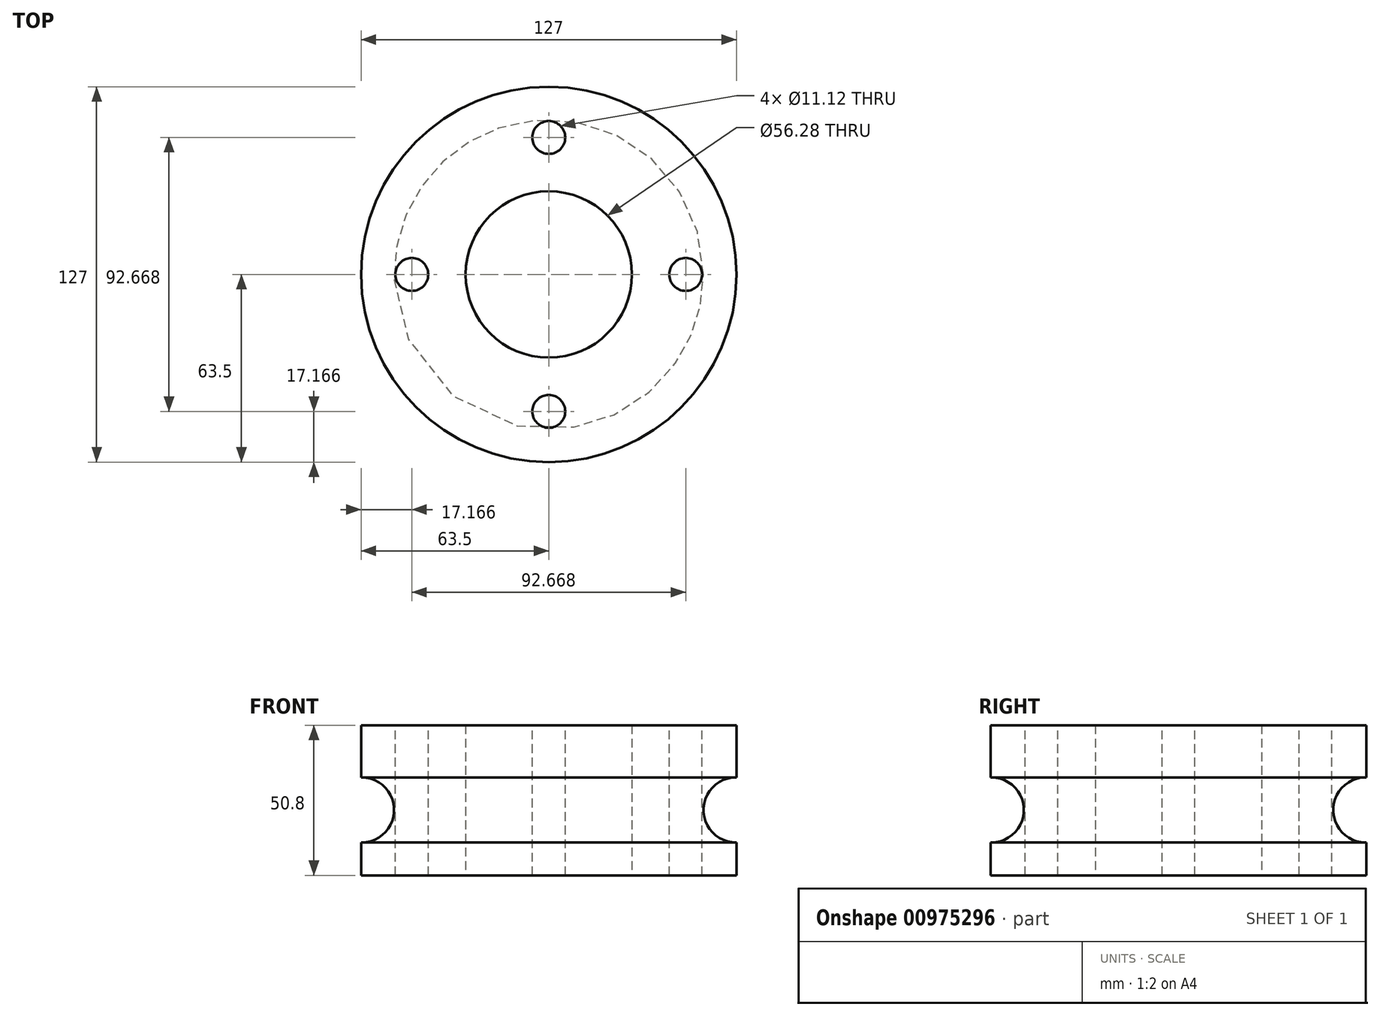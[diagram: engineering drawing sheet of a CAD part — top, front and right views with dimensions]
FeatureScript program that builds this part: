
annotation { "Feature Type Name" : "Feature", "Feature Type Description" : "" }
export const myFeature = defineFeature(function(context is Context, id is Id, definition is map)
    precondition{}
    {
        {
            var Q0;
            Q0=qCreatedBy(makeId("Top.planeOp"),FACE);
            var sketch = newSketch(context, id + "F0", { "sketchPlane" : qUnion([Q0])});
            skCircle(sketch, "E0", {"center": v(0, 0) * mm, "radius": 63.5 * mm});
            skCircle(sketch, "E1", {"center": v(0, 0) * mm, "radius": 28.14 * mm});
            skSolve(sketch);
        }
        {
            var Q0;
            Q0 = qSketchRegion(id + "F0", true);
            extrude(context, id + "F1", {"entities" : qUnion([Q0]), "depth" : 50.8 * mm, "offsetDistance" : 25.4 * mm});
        }
        {
            var Q0;
            Q0=qCreatedBy(makeId("Right.planeOp"),FACE);
            var sketch = newSketch(context, id + "F2", { "sketchPlane" : qUnion([Q0])});
            skCircle(sketch, "E2", {"center": v(63.35, 22.13) * mm, "radius": 11.02 * mm});
            skSolve(sketch);
        }
        {
            var Q0;
            Q0=makeQuery(id+"F2.imprint","IMPRINT",FACE,{"disambiguationData":[TD([[makeQuery(id+"F2.imprint","IMPRINT",EDGE,{"derivedFrom":sQuery(id+"F2.wireOp",EDGE,"E2")}),1.0]])]});
            var Q1;
            Q1=makeQuery(id+"F1.opExtrude","CAP_EDGE",EDGE,{"disambiguationData":[OSD([sQuery(id+"F0.wireOp",EDGE,"E0")])],"isStart":false});
            sweep(context, id + "F3", {"operationType" : NewBodyOperationType.REMOVE, "profiles" : qUnion([Q0]), "path" : qUnion([Q1])});
        }
        {
            var Q0;
            Q0=makeQuery(id+"F1.opExtrude","CAP_FACE",FACE,{"disambiguationData":[OSD([sQuery(id+"F0.wireOp",EDGE,"E0"),sQuery(id+"F0.wireOp",EDGE,"E1")])],"isStart":false});
            var sketch = newSketch(context, id + "F4", { "sketchPlane" : qUnion([Q0])});
            skCircle(sketch, "E3", {"center": v(0, -46.33) * mm, "radius": 5.56 * mm});
            skCircle(sketch, "E4.1.0", {"center": v(46.33, 0) * mm, "radius": 5.56 * mm});
            skCircle(sketch, "E4.2.0", {"center": v(0, 46.33) * mm, "radius": 5.56 * mm});
            skCircle(sketch, "E4.3.0", {"center": v(-46.33, 0) * mm, "radius": 5.56 * mm});
            skPoint(sketch, "E4.center", {"position": v(0, 0) * mm});
            skSolve(sketch);
        }
        {
            var Q0;
            Q0 = qSketchRegion(id + "F4", true);
            extrude(context, id + "F5", {"entities" : qUnion([Q0]), "operationType" : NewBodyOperationType.REMOVE, "endBound" : BoundingType.THROUGH_ALL, "oppositeDirection" : true, "depth" : 25.4 * mm, "offsetDistance" : 25.4 * mm});
        }
    });
